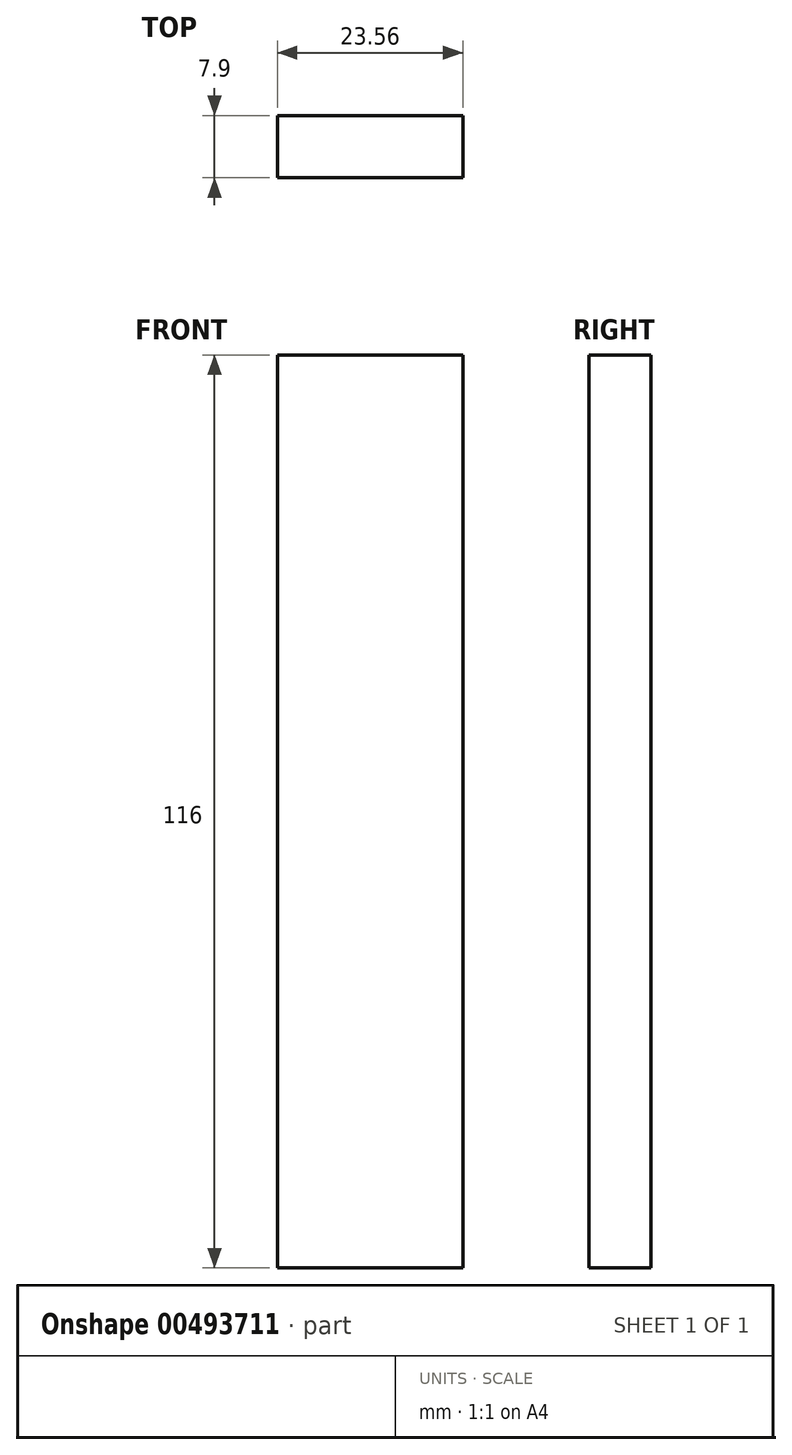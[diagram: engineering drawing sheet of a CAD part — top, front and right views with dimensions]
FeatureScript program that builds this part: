
annotation { "Feature Type Name" : "Feature", "Feature Type Description" : "" }
export const myFeature = defineFeature(function(context is Context, id is Id, definition is map)
    precondition{}
    {
        {
            var Q0;
            Q0=qCreatedBy(makeId("Front.planeOp"),FACE);
            var sketch = newSketch(context, id + "F0", { "sketchPlane" : qUnion([Q0])});
            skLineSegment(sketch, "E0.bottom", {"start": v(-11.78, 58) * mm, "end": v(11.78, 58) * mm});
            skLineSegment(sketch, "E0.top", {"start": v(-11.78, -58) * mm, "end": v(11.78, -58) * mm});
            skLineSegment(sketch, "E0.left", {"start": v(-11.78, 58) * mm, "end": v(-11.78, -58) * mm});
            skLineSegment(sketch, "E0.right", {"start": v(11.78, 58) * mm, "end": v(11.78, -58) * mm});
            skPoint(sketch, "E0.middle", {"position": v(0, 0) * mm});
            skSolve(sketch);
        }
        {
            var Q0;
            Q0=makeQuery(id+"F0.imprint","IMPRINT",FACE,{"disambiguationData":[TD([[makeQuery(id+"F0.imprint","IMPRINT",EDGE,{"derivedFrom":sQuery(id+"F0.wireOp",EDGE,"E0.bottom")}),-1.0]])]});
            extrude(context, id + "F1", {"entities" : qUnion([Q0]), "endBound" : BoundingType.SYMMETRIC, "depth" : 7.9 * mm});
        }
    });
